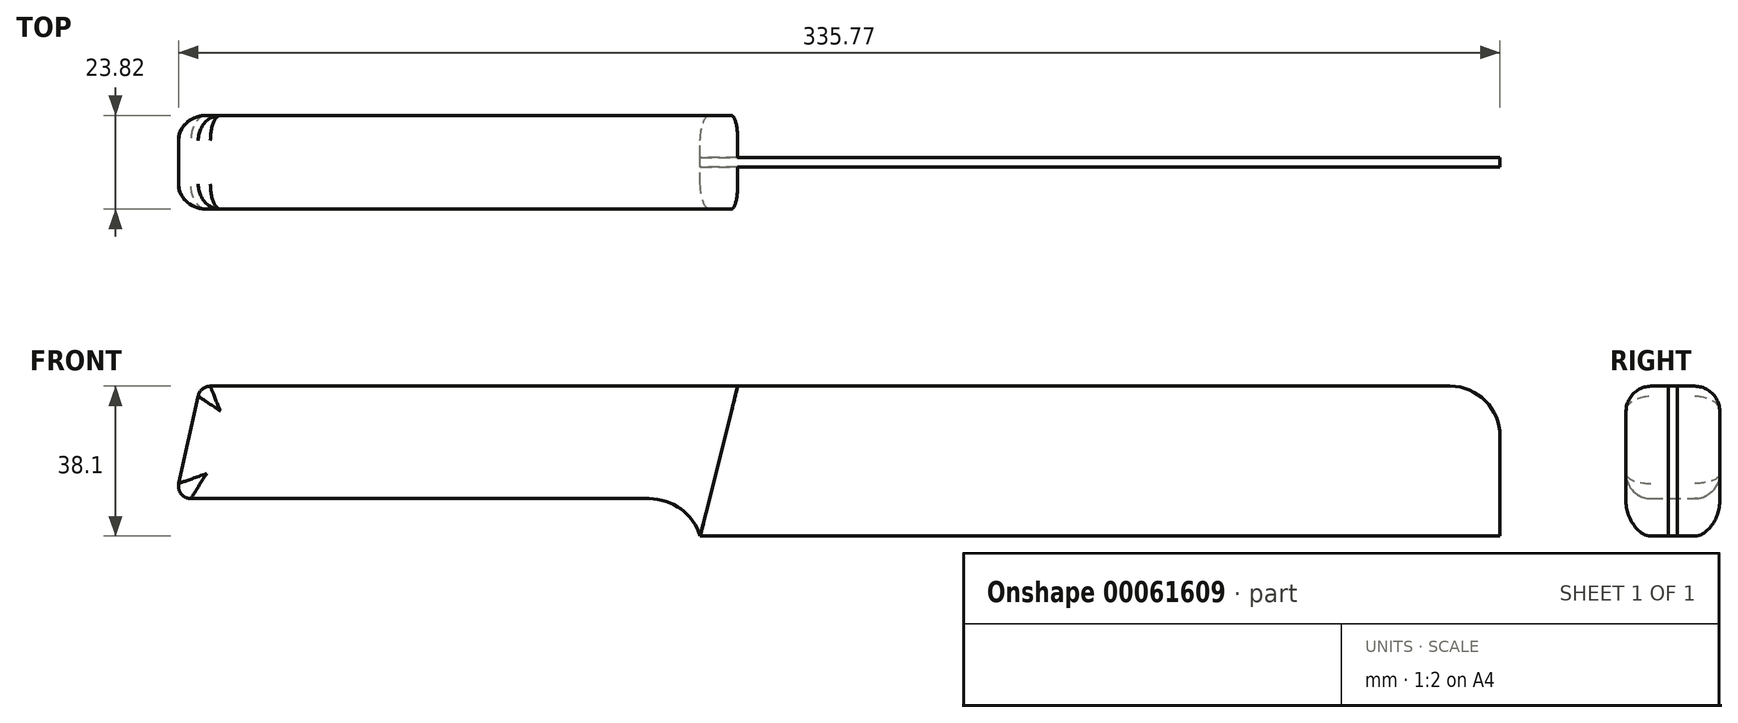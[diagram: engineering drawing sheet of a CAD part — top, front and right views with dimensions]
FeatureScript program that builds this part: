
annotation { "Feature Type Name" : "Feature", "Feature Type Description" : "" }
export const myFeature = defineFeature(function(context is Context, id is Id, definition is map)
    precondition{}
    {
        {
            var Q0;
            Q0=qCreatedBy(makeId("Front.planeOp"),FACE);
            var sketch = newSketch(context, id + "F0", { "sketchPlane" : qUnion([Q0])});
            skLineSegment(sketch, "E0.bottom", {"start": v(0, -19.05) * mm, "end": v(203.2, -19.05) * mm});
            skLineSegment(sketch, "E0.top", {"start": v(0, 19.05) * mm, "end": v(190.5, 19.05) * mm});
            skLineSegment(sketch, "E0.left", {"start": v(0, -19.05) * mm, "end": v(0, 19.05) * mm});
            skLineSegment(sketch, "E0.right", {"start": v(203.2, -19.05) * mm, "end": v(203.2, 6.35) * mm});
            skLineSegment(sketch, "E1", {"start": v(-104.01, 0) * mm, "end": v(0, 0) * mm, "construction": true});
            skPoint(sketch, "E2.visualSharp", {"position": v(203.2, 19.05) * mm});
            skArc(sketch, "E2.filletArc", {"start": v(203.2, 6.35) * mm, "mid": v(199.48, 15.33) * mm, "end": v(190.5, 19.05) * mm});
            skSolve(sketch);
        }
        {
            var Q0;
            Q0 = qSketchRegion(id + "F0", true);
            extrude(context, id + "F1", {"entities" : qUnion([Q0]), "endBound" : BoundingType.SYMMETRIC, "depth" : 2.38 * mm});
        }
        {
            var Q0;
            Q0=qCreatedBy(makeId("Front.planeOp"),FACE);
            var sketch = newSketch(context, id + "F2", { "sketchPlane" : qUnion([Q0])});
            skLineSegment(sketch, "E3", {"start": v(0, -19.05) * mm, "end": v(9.53, 19.05) * mm});
            skLineSegment(sketch, "E4", {"start": v(9.52, 19.05) * mm, "end": v(-124.45, 19.05) * mm});
            skLineSegment(sketch, "E5", {"start": v(-127.55, 16.56) * mm, "end": v(-132.5, -5.66) * mm});
            skLineSegment(sketch, "E6", {"start": v(-129.4, -9.53) * mm, "end": v(-12.99, -9.52) * mm});
            skArc(sketch, "E7", {"start": v(-12.99, -9.52) * mm, "mid": v(-4.93, -12.16) * mm, "end": v(0, -19.05) * mm});
            skPoint(sketch, "E8.visualSharp", {"position": v(-127, 19.05) * mm});
            skArc(sketch, "E8.filletArc", {"start": v(-124.45, 19.05) * mm, "mid": v(-126.44, 18.35) * mm, "end": v(-127.55, 16.56) * mm});
            skPoint(sketch, "E9.visualSharp", {"position": v(-133.35, -9.53) * mm});
            skArc(sketch, "E9.filletArc", {"start": v(-132.5, -5.66) * mm, "mid": v(-131.87, -8.34) * mm, "end": v(-129.4, -9.53) * mm});
            skSolve(sketch);
        }
        {
            var Q0;
            Q0 = qSketchRegion(id + "F2", true);
            extrude(context, id + "F3", {"entities" : qUnion([Q0]), "operationType" : NewBodyOperationType.ADD, "endBound" : BoundingType.SYMMETRIC, "depth" : 23.8 * mm});
        }
        {
            var Q0;
            Q0=makeQuery(id+"F3.opExtrude","CAP_EDGE",EDGE,{"disambiguationData":[OSD([sQuery(id+"F2.wireOp",EDGE,"E4")])],"isStart":true});
            var Q1;
            Q1=makeQuery(id+"F3.opExtrude","CAP_EDGE",EDGE,{"disambiguationData":[OSD([sQuery(id+"F2.wireOp",EDGE,"E4")])],"isStart":false});
            fillet(context, id + "F4", {"entities" : qUnion([Q0, Q1]), "radius" : 6.35 * mm, "tangentPropagation" : true, "allowEdgeOverflow" : false});
        }
    });
